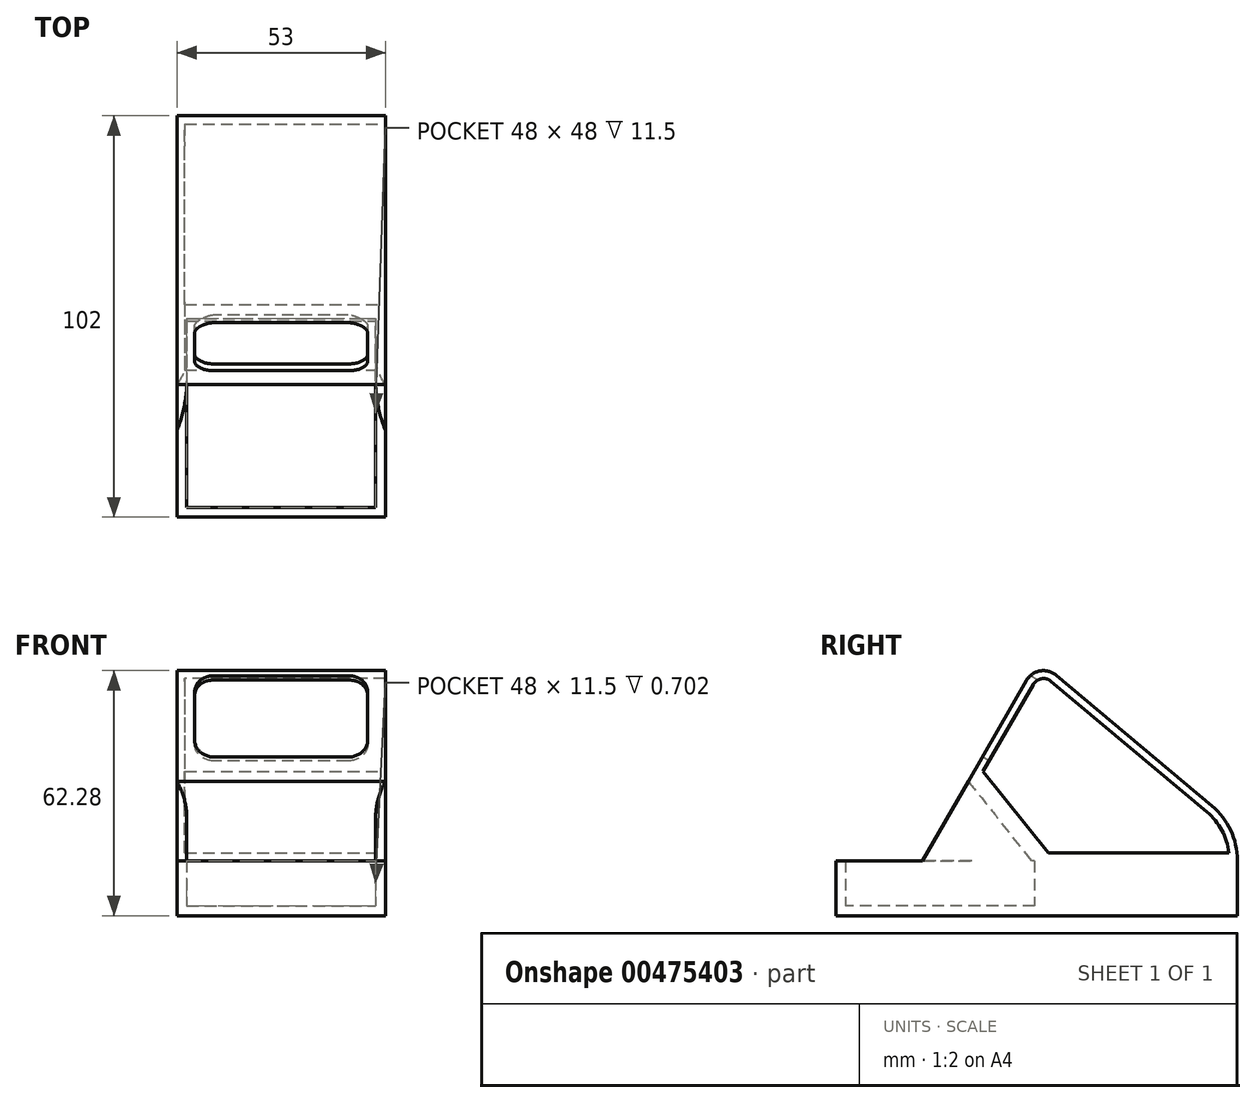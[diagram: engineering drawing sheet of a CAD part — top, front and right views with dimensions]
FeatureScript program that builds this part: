
annotation { "Feature Type Name" : "Feature", "Feature Type Description" : "" }
export const myFeature = defineFeature(function(context is Context, id is Id, definition is map)
    precondition{}
    {
        {
            var Q0;
            Q0=qCreatedBy(makeId("Top.planeOp"),FACE);
            var sketch = newSketch(context, id + "F0", { "sketchPlane" : qUnion([Q0])});
            skLineSegment(sketch, "E0.bottom", {"start": v(-26.5, 51) * mm, "end": v(26.5, 51) * mm});
            skLineSegment(sketch, "E0.top", {"start": v(-26.5, -51) * mm, "end": v(26.5, -51) * mm});
            skLineSegment(sketch, "E0.left", {"start": v(-26.5, 51) * mm, "end": v(-26.5, -51) * mm});
            skLineSegment(sketch, "E0.right", {"start": v(26.5, 51) * mm, "end": v(26.5, -51) * mm});
            skPoint(sketch, "E0.middle", {"position": v(0, 0) * mm});
            skPoint(sketch, "E1.endSnap0", {"position": v(0, -51) * mm});
            skLineSegment(sketch, "E2", {"start": v(-26.5, 2) * mm, "end": v(26.5, 2) * mm});
            skSolve(sketch);
        }
        {
            var Q0;
            {var subQ0=sQuery(id+"F0.wireOp",EDGE,"E0.top");Q0=makeQuery(id+"F0.imprint","IMPRINT",FACE,{"disambiguationData":[TD([[makeQuery(id+"F0.imprint","IMPRINT",EDGE,{"derivedFrom":subQ0}),1.0]])]});}
            extrude(context, id + "F1", {"entities" : qUnion([Q0]), "depth" : 14 * mm});
        }
        {
            var Q0;
            {var subQ0=sQuery(id+"F0.wireOp",EDGE,"E0.bottom");Q0=makeQuery(id+"F0.imprint","IMPRINT",FACE,{"disambiguationData":[TD([[makeQuery(id+"F0.imprint","IMPRINT",EDGE,{"derivedFrom":subQ0}),-1.0]])]});}
            extrude(context, id + "F2", {"entities" : qUnion([Q0]), "depth" : 14 * mm});
        }
        {
            var Q0;
            Q0=makeQuery(id+"F1.opExtrude","CAP_FACE",FACE,{"disambiguationData":[OSD([sQuery(id+"F0.wireOp",EDGE,"E0.top"),sQuery(id+"F0.wireOp",EDGE,"E0.left"),sQuery(id+"F0.wireOp",EDGE,"E0.right"),sQuery(id+"F0.wireOp",EDGE,"E2")])],"isStart":false});
            shell(context, id + "F3", {"entities" : qUnion([Q0]), "thickness" : 2.5 * mm});
        }
        {
            var Q0;
            Q0=makeQuery(id+"F2.opExtrude","SWEPT_FACE",FACE,{"disambiguationData":[OSD([sQuery(id+"F0.wireOp",EDGE,"E0.right")])]});
            var sketch = newSketch(context, id + "F4", { "sketchPlane" : qUnion([Q0])});
            skLineSegment(sketch, "E3.0.0", {"start": v(-51, 0) * mm, "end": v(2, 0) * mm});
            skLineSegment(sketch, "E3.0.1", {"start": v(2, 0) * mm, "end": v(2, 14) * mm});
            skLineSegment(sketch, "E3.0.2", {"start": v(2, 14) * mm, "end": v(-51, 14) * mm});
            skLineSegment(sketch, "E3.0.3", {"start": v(-51, 14) * mm, "end": v(-51, 0) * mm});
            skLineSegment(sketch, "E4.0.0", {"start": v(2, 0) * mm, "end": v(51, 0) * mm});
            skLineSegment(sketch, "E4.0.1", {"start": v(51, 0) * mm, "end": v(51, 14) * mm});
            skLineSegment(sketch, "E4.0.2", {"start": v(51, 14) * mm, "end": v(2, 14) * mm});
            skLineSegment(sketch, "E4.0.3", {"start": v(2, 14) * mm, "end": v(2, 0) * mm});
            skLineSegment(sketch, "E5", {"start": v(-51, 14) * mm, "end": v(-16, 14) * mm});
            skLineSegment(sketch, "E6", {"start": v(51, 0) * mm, "end": v(51, 22.5) * mm});
            skLineSegment(sketch, "E7", {"start": v(51, 22.5) * mm, "end": v(0.42, 64.94) * mm});
            skLineSegment(sketch, "E8", {"start": v(-16, 14) * mm, "end": v(-16, 36.5) * mm});
            skLineSegment(sketch, "E9", {"start": v(-16, 36.5) * mm, "end": v(0.42, 64.94) * mm});
            skLineSegment(sketch, "E10", {"start": v(-16, 36.5) * mm, "end": v(2, 14) * mm});
            skLineSegment(sketch, "E11", {"start": v(-16, 36.5) * mm, "end": v(-29, 14) * mm});
            skSolve(sketch);
        }
        {
            var Q0;
            {var subQ2=sQuery(id+"F4.wireOp",EDGE,"E4.0.2");Q0=makeQuery(id+"F4.imprint","IMPRINT",FACE,{"disambiguationData":[TD([[makeQuery(id+"F4.imprint","IMPRINT",EDGE,{"derivedFrom":subQ2}),-1.0]])]});}
            var Q1;
            Q1=makeQuery(id+"F2.opExtrude","SWEPT_FACE",FACE,{"disambiguationData":[OSD([sQuery(id+"F0.wireOp",EDGE,"E0.left")])]});
            extrude(context, id + "F5", {"entities" : qUnion([Q0]), "endBound" : BoundingType.UP_TO_SURFACE, "oppositeDirection" : true, "endBoundEntityFace" : qUnion([Q1]), "depth" : 25 * mm});
        }
        {
            var Q0;
            Q0=makeQuery(id+"F4.imprint","IMPRINT",FACE,{"disambiguationData":[TD([[makeQuery(id+"F4.imprint","IMPRINT",EDGE,{"derivedFrom":sQuery(id+"F4.wireOp",EDGE,"E3.0.2")}),-1.0]])]});
            var Q1;
            {var subQ0=sQuery(id+"F4.wireOp",EDGE,"E8");Q1=makeQuery(id+"F4.imprint","IMPRINT",FACE,{"disambiguationData":[TD([[makeQuery(id+"F4.imprint","IMPRINT",EDGE,{"derivedFrom":subQ0}),1.0]])]});}
            var Q2;
            {var subQ0=sQuery(id+"F0.wireOp",EDGE,"E0.left");Q2=makeQuery(id+"F5.boolean.opBoolean","MERGE",FACE,{"derivedFrom":[makeQuery(id+"F2.opExtrude","SWEPT_FACE",FACE,{"disambiguationData":[OSD([subQ0])]}),makeQuery(id+"F5.opExtrude","CAP_FACE",FACE,{"disambiguationData":[OSD([subQ0])],"isStart":false})]});}
            extrude(context, id + "F6", {"entities" : qUnion([Q0, Q1]), "endBound" : BoundingType.UP_TO_SURFACE, "oppositeDirection" : true, "endBoundEntityFace" : qUnion([Q2]), "depth" : 25 * mm});
        }
        {
            var Q0;
            Q0=makeQuery(id+"F6.opExtrude","SWEPT_FACE",FACE,{"disambiguationData":[OSD([sQuery(id+"F4.wireOp",EDGE,"E11")])]});
            var Q1;
            Q1=makeQuery(id+"F6.opExtrude","SWEPT_FACE",FACE,{"disambiguationData":[OSD([sQuery(id+"F4.wireOp",EDGE,"E3.0.2"),sQuery(id+"F4.wireOp",EDGE,"E5")])]});
            shell(context, id + "F7", {"entities" : qUnion([Q0, Q1]), "thickness" : 2.5 * mm});
        }
        {
            var Q0;
            Q0=makeQuery(id+"F5.opExtrude","SWEPT_FACE",FACE,{"disambiguationData":[OSD([sQuery(id+"F4.wireOp",EDGE,"E9")])]});
            var sketch = newSketch(context, id + "F8", { "sketchPlane" : qUnion([Q0])});
            skLineSegment(sketch, "E12.0.0", {"start": v(26.5, 56.45) * mm, "end": v(-26.5, 56.45) * mm});
            skLineSegment(sketch, "E12.0.1", {"start": v(-26.5, 56.45) * mm, "end": v(-26.5, 23.6) * mm});
            skLineSegment(sketch, "E12.0.2", {"start": v(-26.5, 23.6) * mm, "end": v(26.5, 23.6) * mm});
            skLineSegment(sketch, "E12.0.3", {"start": v(26.5, 23.6) * mm, "end": v(26.5, 56.45) * mm});
            skLineSegment(sketch, "E13.bottom", {"start": v(-17, 52.03) * mm, "end": v(17, 52.03) * mm});
            skLineSegment(sketch, "E13.top", {"start": v(-17, 28.03) * mm, "end": v(17, 28.03) * mm});
            skLineSegment(sketch, "E13.left", {"start": v(-22, 47.03) * mm, "end": v(-22, 33.03) * mm});
            skLineSegment(sketch, "E13.right", {"start": v(22, 47.03) * mm, "end": v(22, 33.03) * mm});
            skPoint(sketch, "E13.middle", {"position": v(0, 40.03) * mm});
            skPoint(sketch, "E13.middle.positionSnap0", {"position": v(-26.5, 40.03) * mm});
            skPoint(sketch, "E13.middle.positionSnap1", {"position": v(0, 56.45) * mm});
            skPoint(sketch, "E13.centerSnap0", {"position": v(-26.5, 40.03) * mm});
            skPoint(sketch, "E13.centerSnap1", {"position": v(0, 56.45) * mm});
            skPoint(sketch, "E14.visualSharp", {"position": v(-22, 52.03) * mm});
            skArc(sketch, "E14.filletArc", {"start": v(-17, 52.03) * mm, "mid": v(-20.54, 50.57) * mm, "end": v(-22, 47.03) * mm});
            skPoint(sketch, "E15.visualSharp", {"position": v(-22, 28.03) * mm});
            skArc(sketch, "E15.filletArc", {"start": v(-22, 33.03) * mm, "mid": v(-20.54, 29.5) * mm, "end": v(-17, 28.03) * mm});
            skPoint(sketch, "E16.visualSharp", {"position": v(22, 28.03) * mm});
            skArc(sketch, "E16.filletArc", {"start": v(17, 28.03) * mm, "mid": v(20.54, 29.5) * mm, "end": v(22, 33.03) * mm});
            skPoint(sketch, "E17.visualSharp", {"position": v(22, 52.03) * mm});
            skArc(sketch, "E17.filletArc", {"start": v(22, 47.03) * mm, "mid": v(20.54, 50.57) * mm, "end": v(17, 52.03) * mm});
            skSolve(sketch);
        }
        {
            var Q0;
            Q0=makeQuery(id+"F5.opExtrude","SWEPT_EDGE",EDGE,{"disambiguationData":[OSD([sQuery(id+"F4.wireOp",EDGE,"E6"),sQuery(id+"F4.wireOp",EDGE,"E7")])]});
            fillet(context, id + "F9", {"entities" : qUnion([Q0]), "radius" : 18 * mm, "tangentPropagation" : true, "allowEdgeOverflow" : false});
        }
        {
            var Q0;
            Q0=makeQuery(id+"F5.opExtrude","SWEPT_EDGE",EDGE,{"disambiguationData":[OSD([sQuery(id+"F4.wireOp",EDGE,"E7"),sQuery(id+"F4.wireOp",EDGE,"E9")])]});
            fillet(context, id + "F10", {"entities" : qUnion([Q0]), "radius" : 5 * mm, "tangentPropagation" : true, "allowEdgeOverflow" : false});
        }
        {
            var Q0;
            Q0=makeQuery(id+"F5.opExtrude","CAP_FACE",FACE,{"disambiguationData":[OSD([sQuery(id+"F4.wireOp",EDGE,"E4.0.2"),sQuery(id+"F4.wireOp",EDGE,"E6"),sQuery(id+"F4.wireOp",EDGE,"E7"),sQuery(id+"F4.wireOp",EDGE,"E9"),sQuery(id+"F4.wireOp",EDGE,"E10")])],"isStart":true});
            shell(context, id + "F11", {"entities" : qUnion([Q0]), "thickness" : 2 * mm});
        }
        {
            var Q0;
            Q0=makeQuery(id+"F8.imprint","IMPRINT",FACE,{"disambiguationData":[TD([[makeQuery(id+"F8.imprint","IMPRINT",EDGE,{"derivedFrom":sQuery(id+"F8.wireOp",EDGE,"E13.bottom")}),-1.0]])]});
            extrude(context, id + "F12", {"entities" : qUnion([Q0]), "operationType" : NewBodyOperationType.REMOVE, "oppositeDirection" : true, "depth" : 7.2 * mm});
        }
        {
            var Q0;
            Q0=makeQuery(id+"F6.opExtrude","SWEPT_BODY",BODY,{"disambiguationData":[OSD([sQuery(id+"F4.wireOp",EDGE,"E3.0.2"),sQuery(id+"F4.wireOp",EDGE,"E5"),sQuery(id+"F4.wireOp",EDGE,"E10"),sQuery(id+"F4.wireOp",EDGE,"E11")])]});
            var Q1;
            Q1=makeQuery(id+"F5.opExtrude","SWEPT_BODY",BODY,{"disambiguationData":[OSD([sQuery(id+"F4.wireOp",EDGE,"E4.0.2"),sQuery(id+"F4.wireOp",EDGE,"E6"),sQuery(id+"F4.wireOp",EDGE,"E7"),sQuery(id+"F4.wireOp",EDGE,"E9"),sQuery(id+"F4.wireOp",EDGE,"E10")])]});
            var Q2;
            Q2=makeQuery(id+"F2.opExtrude","SWEPT_BODY",BODY,{"disambiguationData":[OSD([sQuery(id+"F0.wireOp",EDGE,"E0.bottom"),sQuery(id+"F0.wireOp",EDGE,"E0.left"),sQuery(id+"F0.wireOp",EDGE,"E0.right"),sQuery(id+"F0.wireOp",EDGE,"E2")])]});
            var Q3;
            Q3=makeQuery(id+"F1.opExtrude","SWEPT_BODY",BODY,{"disambiguationData":[OSD([sQuery(id+"F0.wireOp",EDGE,"E0.top"),sQuery(id+"F0.wireOp",EDGE,"E0.left"),sQuery(id+"F0.wireOp",EDGE,"E0.right"),sQuery(id+"F0.wireOp",EDGE,"E2")])]});
            booleanBodies(context, id + "F13", {"operationType" : BooleanOperationType.UNION, "tools" : qUnion([Q0, Q1, Q2, Q3])});
        }
        {
            var Q0;
            Q0=makeQuery(id+"F7.opShell","OFFSET_EDGE",EDGE,{"disambiguationData":[OSD([sQuery(id+"F4.wireOp",EDGE,"E5"),sQuery(id+"F4.wireOp",EDGE,"E11")])]});
            var Q1;
            Q1=makeQuery(id+"F6.opExtrude","SWEPT_EDGE",EDGE,{"disambiguationData":[OSD([sQuery(id+"F4.wireOp",EDGE,"E5"),sQuery(id+"F4.wireOp",EDGE,"E11")])]});
            fillet(context, id + "F14", {"entities" : qUnion([Q0, Q1]), "radius" : 25 * mm, "tangentPropagation" : true, "allowEdgeOverflow" : false});
        }
    });
